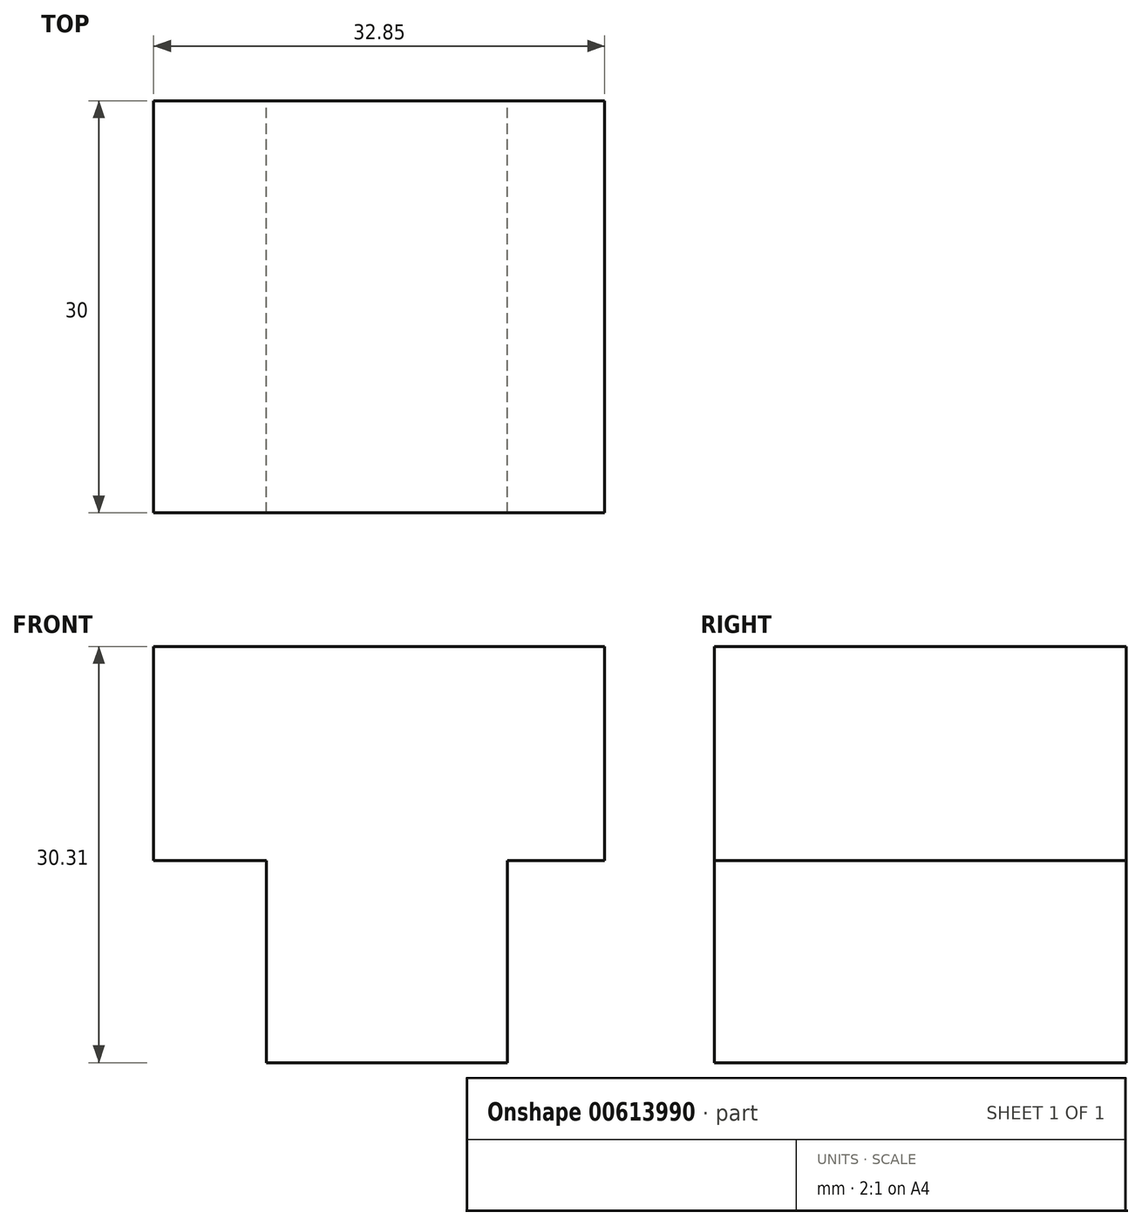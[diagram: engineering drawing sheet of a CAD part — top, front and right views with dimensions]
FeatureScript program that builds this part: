
annotation { "Feature Type Name" : "Feature", "Feature Type Description" : "" }
export const myFeature = defineFeature(function(context is Context, id is Id, definition is map)
    precondition{}
    {
        {
            var Q0;
            Q0=qCreatedBy(makeId("Front.planeOp"),FACE);
            var sketch = newSketch(context, id + "F0", { "sketchPlane" : qUnion([Q0])});
            skLineSegment(sketch, "E0", {"start": v(-16, 36.12) * mm, "end": v(-16, 20.54) * mm});
            skLineSegment(sketch, "E1", {"start": v(-16, 20.54) * mm, "end": v(16.85, 20.54) * mm});
            skLineSegment(sketch, "E2", {"start": v(16.85, 20.54) * mm, "end": v(16.85, 36.12) * mm});
            skLineSegment(sketch, "E3", {"start": v(16.85, 36.12) * mm, "end": v(-16, 36.12) * mm});
            skLineSegment(sketch, "E4", {"start": v(-7.8, 20.54) * mm, "end": v(-7.8, 5.8) * mm});
            skLineSegment(sketch, "E5", {"start": v(-7.8, 5.8) * mm, "end": v(9.77, 5.8) * mm});
            skLineSegment(sketch, "E6", {"start": v(9.77, 5.8) * mm, "end": v(9.77, 20.54) * mm});
            skSolve(sketch);
        }
        {
            var Q0;
            Q0 = qSketchRegion(id + "F0", true);
            extrude(context, id + "F1", {"entities" : qUnion([Q0]), "depth" : 30 * mm, "offsetDistance" : 25 * mm});
        }
    });
